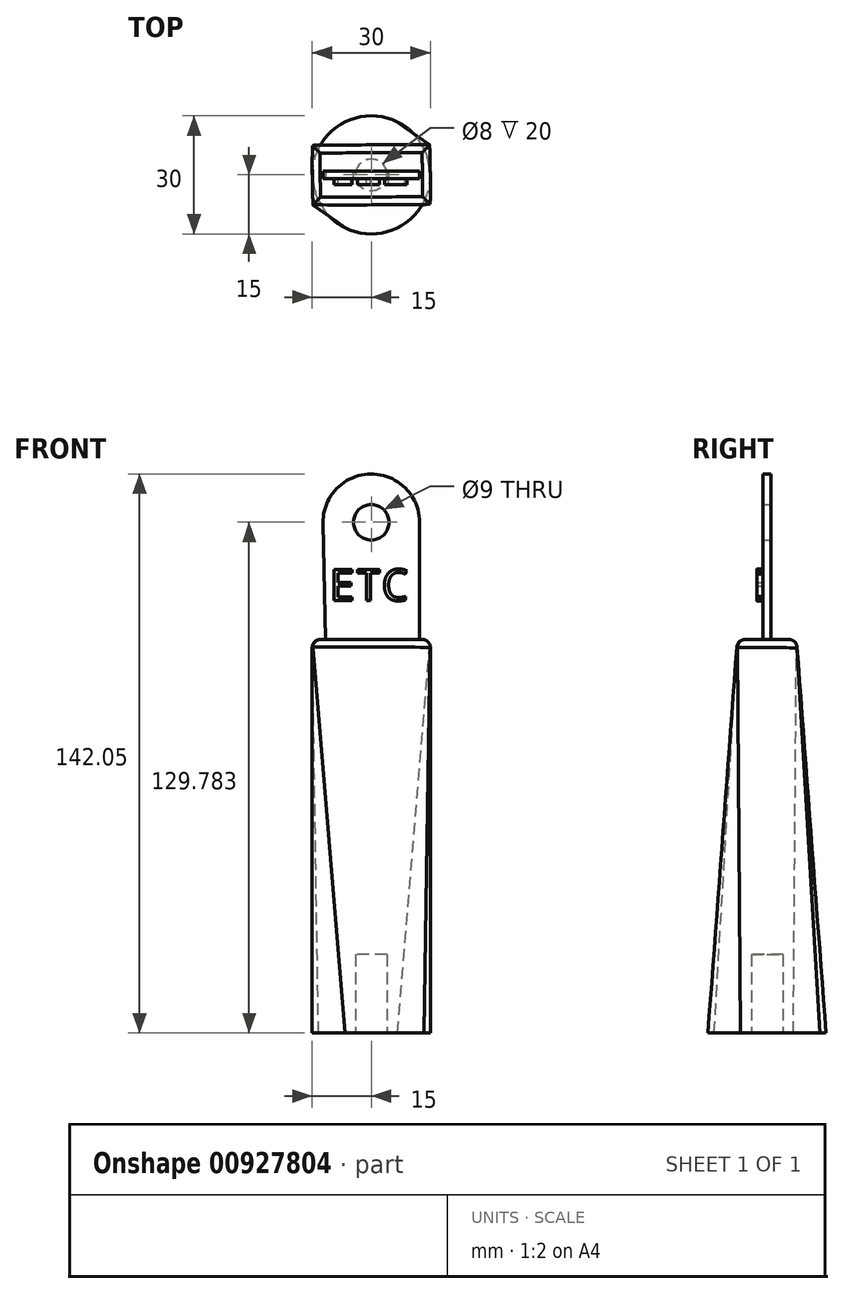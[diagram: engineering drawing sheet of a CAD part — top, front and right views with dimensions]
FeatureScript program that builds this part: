
annotation { "Feature Type Name" : "Feature", "Feature Type Description" : "" }
export const myFeature = defineFeature(function(context is Context, id is Id, definition is map)
    precondition{}
    {
        {
            var Q0;
            Q0=qCreatedBy(makeId("Top.planeOp"),FACE);
            var sketch = newSketch(context, id + "F0", { "sketchPlane" : qUnion([Q0])});
            skCircle(sketch, "E0", {"center": v(0, 0) * mm, "radius": 15 * mm});
            skSolve(sketch);
        }
        {
            var Q0;
            Q0=qCreatedBy(makeId("Top.planeOp"),FACE);
            cPlane(context, id + "F1", {"entities" : qUnion([Q0]), "cplaneType" : CPlaneType.OFFSET, "offset" : 100 * mm, "width" : 150 * mm, "height" : 150 * mm});
        }
        {
            var Q0;
            Q0=qCreatedBy(id+"F1.planeOp",FACE);
            var sketch = newSketch(context, id + "F2", { "sketchPlane" : qUnion([Q0])});
            skLineSegment(sketch, "E1.bottom", {"start": v(15, -7.5) * mm, "end": v(-15, -7.5) * mm});
            skLineSegment(sketch, "E1.top", {"start": v(15, 7.5) * mm, "end": v(-15, 7.5) * mm});
            skLineSegment(sketch, "E1.left", {"start": v(15, -7.5) * mm, "end": v(15, 7.5) * mm});
            skLineSegment(sketch, "E1.right", {"start": v(-15, -7.5) * mm, "end": v(-15, 7.5) * mm});
            skPoint(sketch, "E1.middle", {"position": v(0, 0) * mm});
            skSolve(sketch);
        }
        {
            var Q0;
            Q0=makeQuery(id+"F0.imprint","IMPRINT",FACE,{"disambiguationData":[TD([[makeQuery(id+"F0.imprint","IMPRINT",EDGE,{"derivedFrom":sQuery(id+"F0.wireOp",EDGE,"E0")}),1.0]])]});
            var Q1;
            Q1=makeQuery(id+"F2.imprint","IMPRINT",FACE,{"disambiguationData":[TD([[makeQuery(id+"F2.imprint","IMPRINT",EDGE,{"derivedFrom":sQuery(id+"F2.wireOp",EDGE,"E1.bottom")}),-1.0]])]});
            loft(context, id + "F3", {"sheetProfilesArray" : [{ "sheetProfileEntities" : qUnion([Q0]) }, { "sheetProfileEntities" : qUnion([Q1]) }]});
        }
        {
            var Q0;
            Q0=makeQuery(id+"F3.opLoft","CAP_FACE",FACE,{"disambiguationData":[OSD([makeQuery(id+"F2.imprint","IMPRINT",FACE,{"disambiguationData":[TD([[makeQuery(id+"F2.imprint","IMPRINT",EDGE,{"derivedFrom":sQuery(id+"F2.wireOp",EDGE,"E1.bottom")}),-1.0]])]})])],"isStart":true});
            fillet(context, id + "F4", {"entities" : qUnion([Q0]), "radius" : 2 * mm, "tangentPropagation" : true, "allowEdgeOverflow" : false});
        }
        {
            var Q0;
            Q0=qCreatedBy(makeId("Top.planeOp"),FACE);
            var sketch = newSketch(context, id + "F5", { "sketchPlane" : qUnion([Q0])});
            skCircle(sketch, "E2", {"center": v(0, 0) * mm, "radius": 4 * mm});
            skSolve(sketch);
        }
        {
            var Q0;
            Q0=makeQuery(id+"F5.imprint","IMPRINT",FACE,{"disambiguationData":[TD([[makeQuery(id+"F5.imprint","IMPRINT",EDGE,{"derivedFrom":sQuery(id+"F5.wireOp",EDGE,"E2")}),1.0]])]});
            var Q1;
            Q1=sQuery(id+"F5.wireOp",EDGE,"E2");
            extrude(context, id + "F6", {"entities" : qUnion([Q0]), "operationType" : NewBodyOperationType.REMOVE, "surfaceEntities" : qUnion([Q1]), "depth" : 20 * mm, "offsetDistance" : 25 * mm});
        }
        {
            var Q0;
            Q0=qCreatedBy(makeId("Front.planeOp"),FACE);
            var sketch = newSketch(context, id + "F7", { "sketchPlane" : qUnion([Q0])});
            skCircle(sketch, "E3", {"center": v(0, 129.78) * mm, "radius": 4.5 * mm});
            skCircle(sketch, "E4", {"center": v(0, 129.78) * mm, "radius": 12.27 * mm});
            skLineSegment(sketch, "E5", {"start": v(12.27, 129.78) * mm, "end": v(12.27, 97.89) * mm});
            skLineSegment(sketch, "E6", {"start": v(12.27, 97.89) * mm, "end": v(-11.65, 97.89) * mm});
            skLineSegment(sketch, "E7", {"start": v(-11.65, 97.89) * mm, "end": v(-12.27, 129.78) * mm});
            skSolve(sketch);
        }
        {
            var Q0;
            {var subQ0=sQuery(id+"F7.wireOp",EDGE,"E5");Q0=makeQuery(id+"F7.imprint","IMPRINT",FACE,{"disambiguationData":[TD([[makeQuery(id+"F7.imprint","IMPRINT",EDGE,{"derivedFrom":subQ0}),-1.0]])]});}
            var Q1;
            Q1=makeQuery(id+"F7.imprint","IMPRINT",FACE,{"disambiguationData":[TD([[makeQuery(id+"F7.imprint","IMPRINT",EDGE,{"derivedFrom":sQuery(id+"F7.wireOp",EDGE,"E3")}),-1.0]])]});
            extrude(context, id + "F8", {"entities" : qUnion([Q0, Q1]), "operationType" : NewBodyOperationType.ADD, "endBound" : BoundingType.SYMMETRIC, "depth" : 2 * mm, "offsetDistance" : 25 * mm});
        }
        {
            var Q0;
            Q0=makeQuery(id+"F8.opExtrude","CAP_FACE",FACE,{"disambiguationData":[OSD([sQuery(id+"F7.wireOp",EDGE,"E3"),sQuery(id+"F7.wireOp",EDGE,"E4"),sQuery(id+"F7.wireOp",EDGE,"E5"),sQuery(id+"F7.wireOp",EDGE,"E6"),sQuery(id+"F7.wireOp",EDGE,"E7")])],"isStart":false});
            var sketch = newSketch(context, id + "F9", { "sketchPlane" : qUnion([Q0])});
            skText(sketch, "E8", { "text": "ETC", "fontName": "DroidSansMono.ttf"});
            const initialGuessF9  = {"E8": [-0.0107, 0.10988, 1, 0, 0.008]};
            skSetInitialGuess(sketch, initialGuessF9);
            skSolve(sketch);
        }
        {
            var Q0;
            Q0 = qSketchRegion(id + "F9", true);
            extrude(context, id + "F10", {"entities" : qUnion([Q0]), "operationType" : NewBodyOperationType.ADD, "depth" : 1.5 * mm, "offsetDistance" : 25 * mm});
        }
    });
